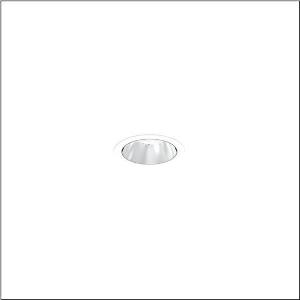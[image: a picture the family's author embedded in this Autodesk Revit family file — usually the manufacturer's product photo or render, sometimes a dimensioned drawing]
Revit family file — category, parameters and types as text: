
# Revit family: lunis_21_s_51db15ta91c
name_source: partatom
category: Lighting Fixtures
units: mm (PartAtom-declared; Revit-internal decimal feet)

## family parameters
Cut with Voids When Loaded = No
Host = Face
Light Source = No
Part Type = Normal
Room Calculation Point = No
Round Connector Dimension = Use Diameter
Shared = No

## types (1)
- --- (1 x LED, 1260 lm, 8 W, 4000K)
    Apparent Load = 8 VA
    CIE Flux Codes = 95 100 100 100 100
    Color Rendering = 80
    Color Temperature = 4000K
    Default Elevation = 1800 mm
    Description = Lunis 21,  S, downlight, light control with lens, of PMMA, anti glare with reflector, of PC, highly specular, light emission: direct distribution, LED rated luminous flux: 960lm, light colour: 8tw, with terminal, 5-pole, mains connection: 220..240V, AC, 50..60Hz, housing, round, of diecast aluminium, traffic white (RAL 9016), diameter: 84mm, clamping range: 1..40mm, protection rating (complete): IP20, protection rating (on room side): IP54, insulation class (complete): insulation class II (safety insulation), certification: CE, impact resistance: IK03, packaging unit: 1 piece
    Height = 0 mm  [stored 0 ft]
    Lamp = 1 x LED
    Lamp Light Flux = 1260 lm
    Lamp Power = 8 W
    Lamp count = 1
    Length = 84 mm
    Luminous efficacy = 158 lm/W
    Manufacturer = Siteco
    ModVariant = No
    Model = 51DB15TA91C
    Mounting Place = Ceiling
    Mounting Type = Recessed
    Number of Poles = 1
    OnlyDefault = Yes
    Power Factor = 1
    Product Name = Lunis 21 S
    Product group = downlight
    ProductGroupID = 400
    Protection Class = Protection class II
    Protection Degree = IP 20
    RLX_Detail_Level = 1
    RLX_Emergency_Light_Flux = 0 lm
    RLX_Emergency_Type = 0
    RLX_Emergency_Type_DB = No
    RlxData = <blob elided: 8461 chars, md5=dba320aa>
    Socket = socket
    Standby Power = 0 W
    System Light Flux = 1260 lm
    System Power = 8 W
    Type Comments = individual setting: colour temperature 4000K, luminous flux: 100 % | (OFF | OFF | ON | OFF) | 200 mA
    Type Image = l_1290840.jpg
    URL = http://relux.com
    VarID = @adj_017871
    Voltage = 0 V
    Weight = 0.00 kg
    Width = 0 mm  [stored 0 ft]

note: [stored X ft] marks values corroborated as IEEE doubles in the binary element streams (Revit-internal decimal feet)

## geometry (parser evidence)
native form markers: Sweep x9
no freeform markers — native parametric forms only
